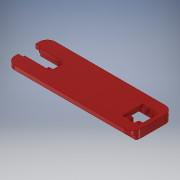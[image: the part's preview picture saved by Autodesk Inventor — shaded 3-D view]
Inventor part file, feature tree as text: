
AUTODESK INVENTOR PART (.ipt)
format: ipt  version: 2019 (Build 230136000, 136)  size: 273,920 bytes
history: native  units: mm
features: extrude x5, sketch x5, chamfer x2, fillet x1
ambient origin geometry x8: Origin, YZ Plane, XZ Plane, XY Plane, X Axis, Y Axis, Z Axis, Center Point
bodies: Solid1 (feature_tree)
feature tree (13):
  extrude  "Extrusion1"  Depth=50.0mm
  extrude  "Extrusion3"  Depth=5.0mm
  extrude  "Extrusion4"  Depth=70.0mm
  chamfer  "Chamfer1"  Distance=5.5mm
  extrude  "Extrusion5"  Depth=70.0mm
  extrude  "Extrusion6"  Depth=5.0mm TaperAngle=0.0deg
  fillet  "Fillet3"  Radius=5.0mm
  chamfer  "Chamfer2"  Distance=25.0mm
  sketch  "Sketch1"  dims[d0=155.0mm d1=50.0mm]
  sketch  "Sketch3"  dims[d2=5.0mm d3=0.0mm d11=5.0mm]
  sketch  "Sketch4"  dims[d12=5.0mm d13=70.0mm]
  sketch  "Sketch6"  dims[d14=9.0mm]
  sketch  "Sketch8"  dims[d15=5.5mm d16=5.5mm d17=70.0mm d18=5.0mm d19=0.0mm d21=5.0mm d22=25.0mm d23=35.0mm d24=5.0mm d25=0.0mm d26=5.0mm d27=2.0mm d28=45.0deg d29=5.0mm d30=5.0mm d31=5.0mm d32=5.0mm d33=5.0mm d34=5.0mm d38=2.2mm d39=2.0mm d40=2.0mm d41=2.2mm d42=2.0mm d43=2.0mm d44=2.2mm d45=2.2mm d46=2.0mm d47=2.0mm d48=2.0mm d49=5.0mm d50=5.0mm d51=14.5mm d52=14.5mm d53=2.0mm d54=20.0mm d55=5.0mm d56=0.0mm d59=31.75mm d60=21.59mm d61=12.5mm d62=12.5mm d67=1.27mm d68=16.51mm d69=3.0mm d70=5.0mm d71=5.0mm d72=5.0mm d73=5.0mm d74=2.0mm d75=2.0mm d76=5.0mm d77=0.0mm d78=10.0mm d79=10.0mm d80=5.0mm d81=45.0deg d82=50.0mm]
